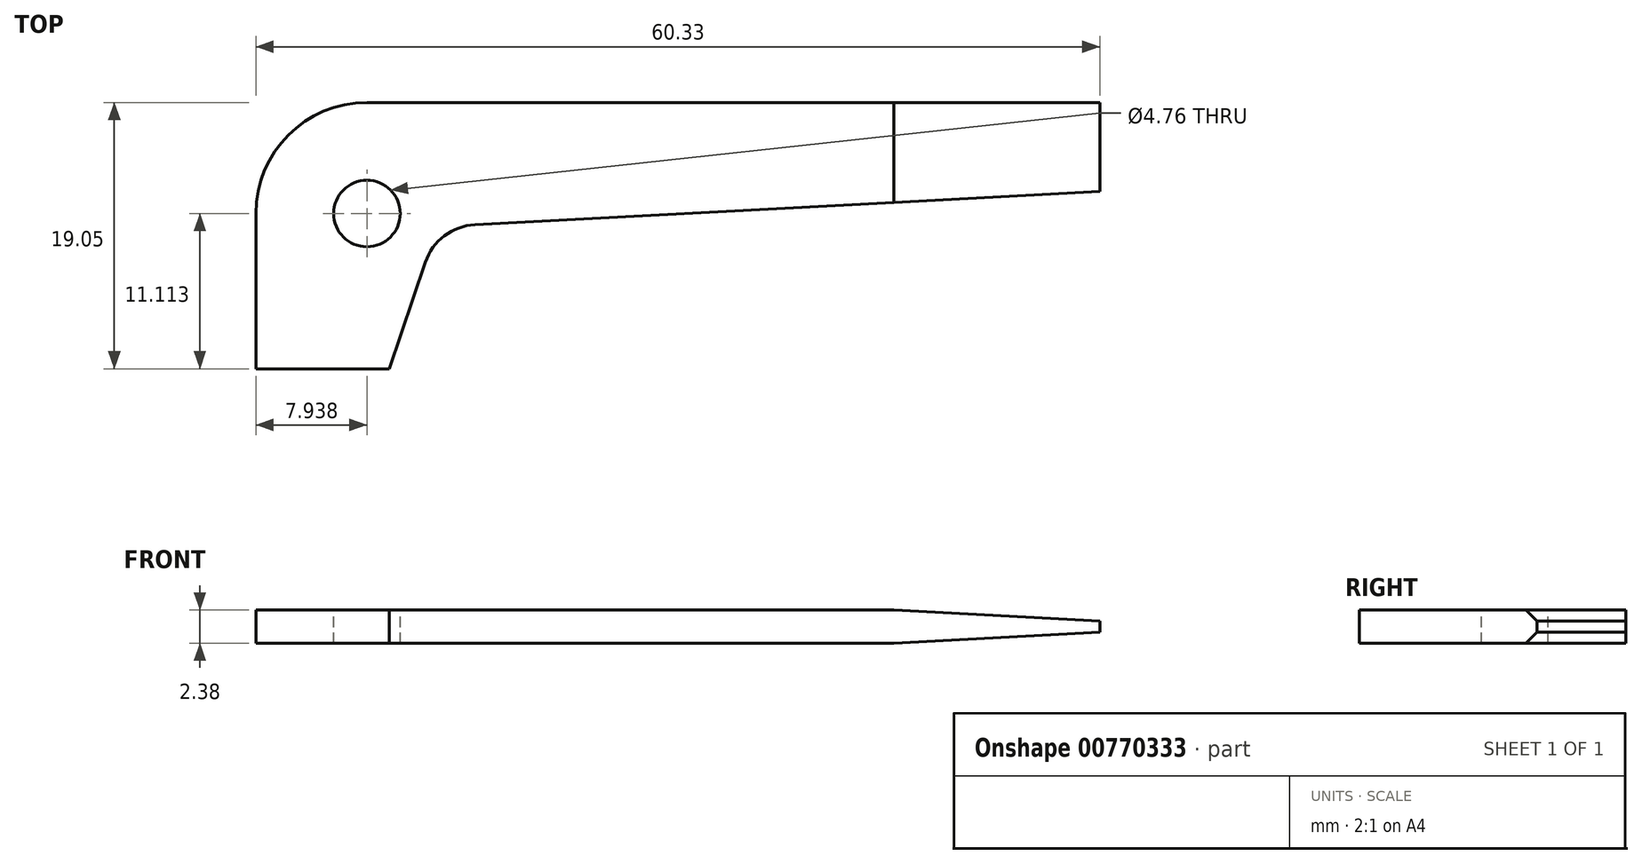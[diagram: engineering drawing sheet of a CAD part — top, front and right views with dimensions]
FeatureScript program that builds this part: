
annotation { "Feature Type Name" : "Feature", "Feature Type Description" : "" }
export const myFeature = defineFeature(function(context is Context, id is Id, definition is map)
    precondition{}
    {
        {
            var Q0;
            Q0=qCreatedBy(makeId("Top.planeOp"),FACE);
            var sketch = newSketch(context, id + "F0", { "sketchPlane" : qUnion([Q0])});
            skLineSegment(sketch, "E0.top", {"start": v(7.94, 19.05) * mm, "end": v(60.33, 19.05) * mm});
            skLineSegment(sketch, "E0.left", {"start": v(0, 0) * mm, "end": v(0, 11.11) * mm});
            skLineSegment(sketch, "E1", {"start": v(9.52, 0) * mm, "end": v(12.12, 7.63) * mm});
            skLineSegment(sketch, "E2", {"start": v(60.33, 12.7) * mm, "end": v(15.66, 10.31) * mm});
            skLineSegment(sketch, "E3", {"start": v(0, 0) * mm, "end": v(9.53, 0) * mm});
            skLineSegment(sketch, "E4", {"start": v(60.33, 12.7) * mm, "end": v(60.33, 19.05) * mm});
            skArc(sketch, "E5", {"start": v(15.66, 10.31) * mm, "mid": v(13.48, 9.51) * mm, "end": v(12.12, 7.63) * mm});
            skPoint(sketch, "E6.visualSharp", {"position": v(0, 19.05) * mm});
            skArc(sketch, "E6.filletArc", {"start": v(7.94, 19.05) * mm, "mid": v(2.32, 16.73) * mm, "end": v(0, 11.11) * mm});
            skSolve(sketch);
        }
        {
            var Q0;
            Q0 = qSketchRegion(id + "F0", true);
            extrude(context, id + "F1", {"entities" : qUnion([Q0]), "depth" : 2.38 * mm, "offsetDistance" : 25.4 * mm});
        }
        {
            var Q0;
            Q0=makeQuery(id+"F1.opExtrude","CAP_FACE",FACE,{"disambiguationData":[OSD([sQuery(id+"F0.wireOp",EDGE,"E0.top"),sQuery(id+"F0.wireOp",EDGE,"E0.left"),sQuery(id+"F0.wireOp",EDGE,"E1"),sQuery(id+"F0.wireOp",EDGE,"E2"),sQuery(id+"F0.wireOp",EDGE,"E3"),sQuery(id+"F0.wireOp",EDGE,"E4"),sQuery(id+"F0.wireOp",EDGE,"E5"),sQuery(id+"F0.wireOp",EDGE,"E6.filletArc")])],"isStart":false});
            var sketch = newSketch(context, id + "F2", { "sketchPlane" : qUnion([Q0])});
            skCircle(sketch, "E7", {"center": v(7.94, 11.11) * mm, "radius": 2.38 * mm});
            skSolve(sketch);
        }
        {
            var Q0;
            Q0 = qSketchRegion(id + "F2", true);
            extrude(context, id + "F3", {"entities" : qUnion([Q0]), "operationType" : NewBodyOperationType.REMOVE, "endBound" : BoundingType.THROUGH_ALL, "oppositeDirection" : true, "depth" : 25.4 * mm, "offsetDistance" : 25.4 * mm});
        }
        {
            var Q0;
            Q0=makeQuery(id+"F1.opExtrude","SWEPT_FACE",FACE,{"disambiguationData":[OSD([sQuery(id+"F0.wireOp",EDGE,"E0.top")])]});
            var sketch = newSketch(context, id + "F4", { "sketchPlane" : qUnion([Q0])});
            skLineSegment(sketch, "E8", {"start": v(-60.33, 2.38) * mm, "end": v(-45.61, 2.38) * mm});
            skLineSegment(sketch, "E9", {"start": v(-60.33, 2.38) * mm, "end": v(-60.33, 1.59) * mm});
            skLineSegment(sketch, "E10", {"start": v(-45.61, 2.38) * mm, "end": v(-60.33, 1.59) * mm});
            skLineSegment(sketch, "E11.MirrorCS", {"start": v(-45.61, 0) * mm, "end": v(-60.33, 0.8) * mm});
            skLineSegment(sketch, "E12.MirrorCS", {"start": v(-60.33, 0) * mm, "end": v(-45.61, 0) * mm});
            skLineSegment(sketch, "E13.MirrorCS", {"start": v(-60.33, 0) * mm, "end": v(-60.33, 0.8) * mm});
            skSolve(sketch);
        }
        {
            var Q0;
            Q0=makeQuery(id+"F4.imprint","IMPRINT",FACE,{"disambiguationData":[TD([[makeQuery(id+"F4.imprint","IMPRINT",EDGE,{"derivedFrom":sQuery(id+"F4.wireOp",EDGE,"E11.MirrorCS")}),1.0]])]});
            var Q1;
            Q1=makeQuery(id+"F4.imprint","IMPRINT",FACE,{"disambiguationData":[TD([[makeQuery(id+"F4.imprint","IMPRINT",EDGE,{"derivedFrom":sQuery(id+"F4.wireOp",EDGE,"E8")}),1.0]])]});
            extrude(context, id + "F5", {"entities" : qUnion([Q0, Q1]), "operationType" : NewBodyOperationType.REMOVE, "oppositeDirection" : true, "depth" : 25.4 * mm, "offsetDistance" : 25.4 * mm});
        }
    });
